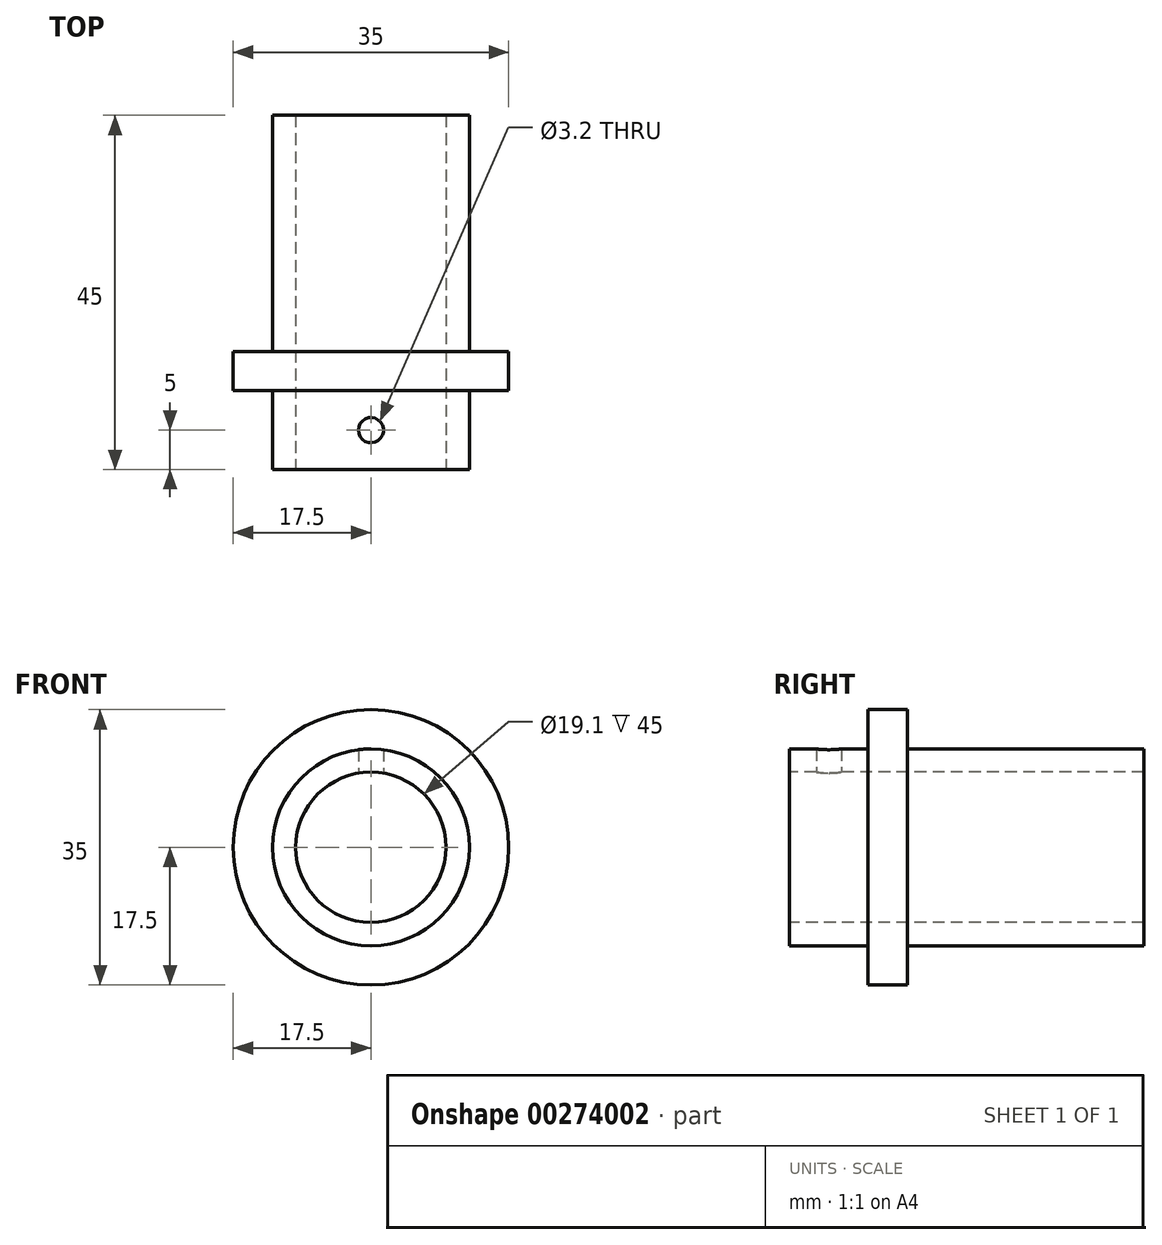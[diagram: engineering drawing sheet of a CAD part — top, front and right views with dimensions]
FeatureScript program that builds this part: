
annotation { "Feature Type Name" : "Feature", "Feature Type Description" : "" }
export const myFeature = defineFeature(function(context is Context, id is Id, definition is map)
    precondition{}
    {
        {
            var Q0;
            Q0=qCreatedBy(makeId("Right.planeOp"),FACE);
            var sketch = newSketch(context, id + "F0", { "sketchPlane" : qUnion([Q0])});
            skLineSegment(sketch, "E0", {"start": v(0, 0) * mm, "end": v(51.68, 0) * mm, "construction": true});
            skLineSegment(sketch, "E1", {"start": v(0, 9.55) * mm, "end": v(45, 9.55) * mm});
            skLineSegment(sketch, "E2", {"start": v(45, 9.55) * mm, "end": v(45, 12.5) * mm});
            skLineSegment(sketch, "E3", {"start": v(45, 12.5) * mm, "end": v(15, 12.5) * mm});
            skLineSegment(sketch, "E4", {"start": v(15, 12.5) * mm, "end": v(15, 17.5) * mm});
            skLineSegment(sketch, "E5", {"start": v(15, 17.5) * mm, "end": v(10, 17.5) * mm});
            skLineSegment(sketch, "E6", {"start": v(10, 17.5) * mm, "end": v(10, 12.5) * mm});
            skLineSegment(sketch, "E7", {"start": v(10, 12.5) * mm, "end": v(0, 12.5) * mm});
            skLineSegment(sketch, "E8", {"start": v(0, 12.5) * mm, "end": v(0, 9.55) * mm});
            skSolve(sketch);
        }
        {
            var Q0;
            Q0=qSketchRegion(id+"F0",true);
            var Q1;
            Q1=sQuery(id+"F0.wireOp",EDGE,"E0");
            revolve(context, id + "F1", {"entities" : qUnion([Q0]), "axis" : qUnion([Q1]), "revolveType" : RevolveType.FULL});
        }
        {
            var Q0;
            Q0=qCreatedBy(makeId("Top.planeOp"),FACE);
            var sketch = newSketch(context, id + "F2", { "sketchPlane" : qUnion([Q0])});
            skCircle(sketch, "E9", {"center": v(0, 5) * mm, "radius": 1.6 * mm});
            skSolve(sketch);
        }
        {
            var Q0;
            Q0=qSketchRegion(id+"F2",true);
            extrude(context, id + "F3", {"entities" : qUnion([Q0]), "operationType" : NewBodyOperationType.REMOVE, "endBound" : BoundingType.THROUGH_ALL, "depth" : 25 * mm});
        }
    });
